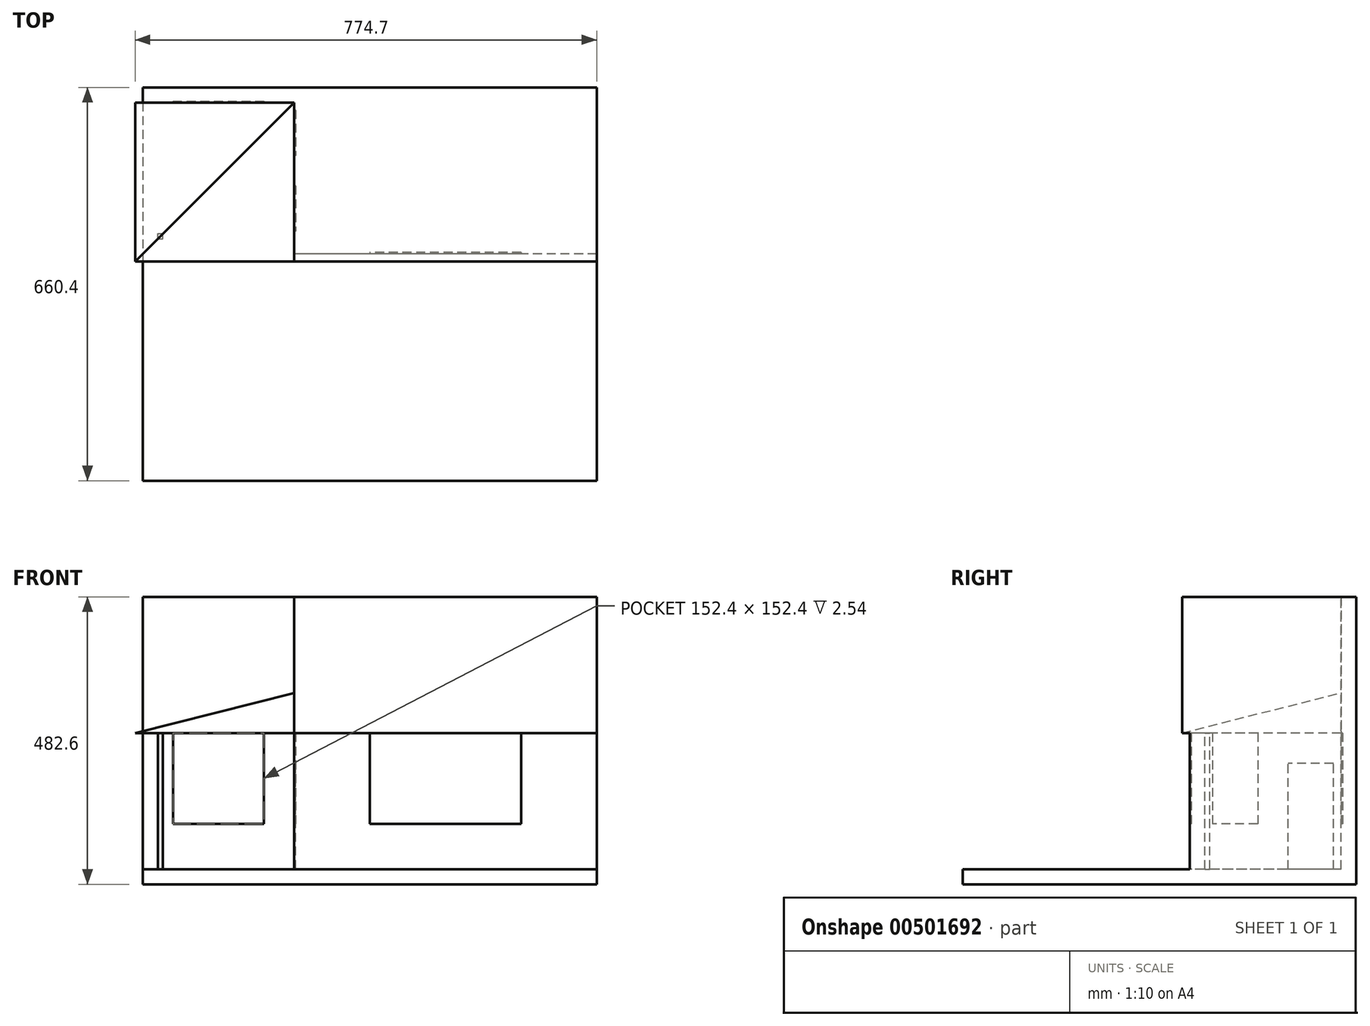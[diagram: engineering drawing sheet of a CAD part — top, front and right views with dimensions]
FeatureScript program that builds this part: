
annotation { "Feature Type Name" : "Feature", "Feature Type Description" : "" }
export const myFeature = defineFeature(function(context is Context, id is Id, definition is map)
    precondition{}
    {
        {
            var Q0;
            Q0=qCreatedBy(makeId("Top.planeOp"),FACE);
            var sketch = newSketch(context, id + "F0", { "sketchPlane" : qUnion([Q0])});
            skLineSegment(sketch, "E0.bottom", {"start": v(381, 330.2) * mm, "end": v(-381, 330.2) * mm});
            skLineSegment(sketch, "E0.top", {"start": v(381, -330.2) * mm, "end": v(-381, -330.2) * mm});
            skLineSegment(sketch, "E0.left", {"start": v(381, 330.2) * mm, "end": v(381, -330.2) * mm});
            skLineSegment(sketch, "E0.right", {"start": v(-381, 330.2) * mm, "end": v(-381, -330.2) * mm});
            skPoint(sketch, "E0.middle", {"position": v(0, 0) * mm});
            skSolve(sketch);
        }
        {
            var Q0;
            Q0 = qSketchRegion(id + "F0", true);
            extrude(context, id + "F1", {"entities" : qUnion([Q0]), "oppositeDirection" : true, "depth" : 25.4 * mm});
        }
        {
            var Q0;
            Q0=makeQuery(id+"F0.imprint","IMPRINT",FACE,{"disambiguationData":[TD([[makeQuery(id+"F0.imprint","IMPRINT",EDGE,{"derivedFrom":sQuery(id+"F0.wireOp",EDGE,"E0.bottom")}),1.0]])]});
            var sketch = newSketch(context, id + "F2", { "sketchPlane" : qUnion([Q0])});
            skLineSegment(sketch, "E1.bottom", {"start": v(381, 330.2) * mm, "end": v(-127, 330.2) * mm});
            skLineSegment(sketch, "E1.top", {"start": v(381, 50.8) * mm, "end": v(-127, 50.8) * mm});
            skLineSegment(sketch, "E1.left", {"start": v(381, 330.2) * mm, "end": v(381, 50.8) * mm});
            skLineSegment(sketch, "E1.right", {"start": v(-127, 330.2) * mm, "end": v(-127, 50.8) * mm});
            skSolve(sketch);
        }
        {
            var Q0;
            Q0 = qSketchRegion(id + "F2", true);
            extrude(context, id + "F3", {"entities" : qUnion([Q0]), "operationType" : NewBodyOperationType.ADD, "depth" : 228.6 * mm});
        }
        {
            var Q0;
            Q0=makeQuery(id+"F3.opExtrude","SWEPT_FACE",FACE,{"disambiguationData":[OSD([sQuery(id+"F2.wireOp",EDGE,"E1.top")])]});
            var sketch = newSketch(context, id + "F4", { "sketchPlane" : qUnion([Q0])});
            skLineSegment(sketch, "E2.bottom", {"start": v(254, 228.6) * mm, "end": v(0, 228.6) * mm});
            skLineSegment(sketch, "E2.top", {"start": v(254, 76.2) * mm, "end": v(0, 76.2) * mm});
            skLineSegment(sketch, "E2.left", {"start": v(254, 228.6) * mm, "end": v(254, 76.2) * mm});
            skLineSegment(sketch, "E2.right", {"start": v(0, 228.6) * mm, "end": v(0, 76.2) * mm});
            skSolve(sketch);
        }
        {
            var Q0;
            Q0 = qSketchRegion(id + "F4", true);
            extrude(context, id + "F5", {"entities" : qUnion([Q0]), "operationType" : NewBodyOperationType.REMOVE, "oppositeDirection" : true, "depth" : 2.54 * mm});
        }
        {
            var Q0;
            Q0=makeQuery(id+"F3.boolean.opBoolean","MERGE",FACE,{"derivedFrom":[makeQuery(id+"F1.opExtrude","SWEPT_FACE",FACE,{"disambiguationData":[OSD([sQuery(id+"F0.wireOp",EDGE,"E0.bottom")])]}),makeQuery(id+"F3.opExtrude","SWEPT_FACE",FACE,{"disambiguationData":[OSD([sQuery(id+"F2.wireOp",EDGE,"E1.bottom")])]})]});
            var sketch = newSketch(context, id + "F6", { "sketchPlane" : qUnion([Q0])});
            skLineSegment(sketch, "E3.bottom", {"start": v(127, 0) * mm, "end": v(381, 0) * mm});
            skLineSegment(sketch, "E3.top", {"start": v(127, 228.6) * mm, "end": v(381, 228.6) * mm});
            skLineSegment(sketch, "E3.left", {"start": v(127, 0) * mm, "end": v(127, 228.6) * mm});
            skLineSegment(sketch, "E3.right", {"start": v(381, 0) * mm, "end": v(381, 228.6) * mm});
            skSolve(sketch);
        }
        {
            var Q0;
            Q0 = qSketchRegion(id + "F6", true);
            extrude(context, id + "F7", {"entities" : qUnion([Q0]), "oppositeDirection" : true, "depth" : 25.4 * mm});
        }
        {
            var Q0;
            Q0=makeQuery(id+"F3.opExtrude","SWEPT_FACE",FACE,{"disambiguationData":[OSD([sQuery(id+"F2.wireOp",EDGE,"E1.right")])]});
            var sketch = newSketch(context, id + "F8", { "sketchPlane" : qUnion([Q0])});
            skLineSegment(sketch, "E4.bottom", {"start": v(-165.1, 228.6) * mm, "end": v(-88.9, 228.6) * mm});
            skLineSegment(sketch, "E4.top", {"start": v(-165.1, 76.2) * mm, "end": v(-88.9, 76.2) * mm});
            skLineSegment(sketch, "E4.left", {"start": v(-165.1, 228.6) * mm, "end": v(-165.1, 76.2) * mm});
            skLineSegment(sketch, "E4.right", {"start": v(-88.9, 228.6) * mm, "end": v(-88.9, 76.2) * mm});
            skLineSegment(sketch, "E5.bottom", {"start": v(-292.1, 0) * mm, "end": v(-215.9, 0) * mm});
            skLineSegment(sketch, "E5.top", {"start": v(-292.1, 177.8) * mm, "end": v(-215.9, 177.8) * mm});
            skLineSegment(sketch, "E5.left", {"start": v(-292.1, 0) * mm, "end": v(-292.1, 177.8) * mm});
            skLineSegment(sketch, "E5.right", {"start": v(-215.9, 0) * mm, "end": v(-215.9, 177.8) * mm});
            skSolve(sketch);
        }
        {
            var Q0;
            Q0 = qSketchRegion(id + "F8", true);
            extrude(context, id + "F9", {"entities" : qUnion([Q0]), "operationType" : NewBodyOperationType.REMOVE, "oppositeDirection" : true, "depth" : 2.54 * mm});
        }
        {
            var Q0;
            Q0=makeQuery(id+"F7.opExtrude","SWEPT_BODY",BODY,{"disambiguationData":[OSD([sQuery(id+"F6.wireOp",EDGE,"E3.bottom"),sQuery(id+"F6.wireOp",EDGE,"E3.top"),sQuery(id+"F6.wireOp",EDGE,"E3.left"),sQuery(id+"F6.wireOp",EDGE,"E3.right")])]});
            var Q1;
            Q1=makeQuery(id+"F1.opExtrude","SWEPT_BODY",BODY,{"disambiguationData":[OSD([sQuery(id+"F0.wireOp",EDGE,"E0.bottom"),sQuery(id+"F0.wireOp",EDGE,"E0.top"),sQuery(id+"F0.wireOp",EDGE,"E0.left"),sQuery(id+"F0.wireOp",EDGE,"E0.right")])]});
            booleanBodies(context, id + "F10", {"operationType" : BooleanOperationType.UNION, "tools" : qUnion([Q0, Q1])});
        }
        {
            var Q0;
            Q0=makeQuery(id+"F7.opExtrude","CAP_FACE",FACE,{"disambiguationData":[OSD([sQuery(id+"F6.wireOp",EDGE,"E3.bottom"),sQuery(id+"F6.wireOp",EDGE,"E3.top"),sQuery(id+"F6.wireOp",EDGE,"E3.left"),sQuery(id+"F6.wireOp",EDGE,"E3.right")])],"isStart":false});
            var sketch = newSketch(context, id + "F11", { "sketchPlane" : qUnion([Q0])});
            skLineSegment(sketch, "E6.bottom", {"start": v(-330.2, 228.6) * mm, "end": v(-177.8, 228.6) * mm});
            skLineSegment(sketch, "E6.top", {"start": v(-330.2, 76.2) * mm, "end": v(-177.8, 76.2) * mm});
            skLineSegment(sketch, "E6.left", {"start": v(-330.2, 228.6) * mm, "end": v(-330.2, 76.2) * mm});
            skLineSegment(sketch, "E6.right", {"start": v(-177.8, 228.6) * mm, "end": v(-177.8, 76.2) * mm});
            skSolve(sketch);
        }
        {
            var Q0;
            Q0 = qSketchRegion(id + "F11", true);
            extrude(context, id + "F12", {"entities" : qUnion([Q0]), "operationType" : NewBodyOperationType.REMOVE, "oppositeDirection" : true, "depth" : 2.54 * mm});
        }
        {
            var Q0;
            Q0=makeQuery(id+"F10.opBoolean","MERGE",FACE,{"derivedFrom":[makeQuery(id+"F7.opExtrude","SWEPT_FACE",FACE,{"disambiguationData":[OSD([sQuery(id+"F6.wireOp",EDGE,"E3.top")])]}),makeQuery(id+"F3.opExtrude","CAP_FACE",FACE,{"disambiguationData":[OSD([sQuery(id+"F2.wireOp",EDGE,"E1.bottom"),sQuery(id+"F2.wireOp",EDGE,"E1.top"),sQuery(id+"F2.wireOp",EDGE,"E1.left"),sQuery(id+"F2.wireOp",EDGE,"E1.right")])],"isStart":false})]});
            var sketch = newSketch(context, id + "F13", { "sketchPlane" : qUnion([Q0])});
            skLineSegment(sketch, "E7.bottom", {"start": v(381, 330.2) * mm, "end": v(-127, 330.2) * mm});
            skLineSegment(sketch, "E7.top", {"start": v(381, 38.1) * mm, "end": v(-127, 38.1) * mm});
            skLineSegment(sketch, "E7.left", {"start": v(381, 330.2) * mm, "end": v(381, 38.1) * mm});
            skLineSegment(sketch, "E7.right", {"start": v(-127, 330.2) * mm, "end": v(-127, 38.1) * mm});
            skSolve(sketch);
        }
        {
            var Q0;
            Q0 = qSketchRegion(id + "F13", true);
            extrude(context, id + "F14", {"entities" : qUnion([Q0]), "operationType" : NewBodyOperationType.ADD, "depth" : 228.6 * mm});
        }
        {
            var Q0;
            Q0=makeQuery(id+"F14.boolean.opBoolean","MERGE",FACE,{"derivedFrom":[makeQuery(id+"F3.opExtrude","SWEPT_FACE",FACE,{"disambiguationData":[OSD([sQuery(id+"F2.wireOp",EDGE,"E1.right")])]}),makeQuery(id+"F14.opExtrude","SWEPT_FACE",FACE,{"disambiguationData":[OSD([sQuery(id+"F13.wireOp",EDGE,"E7.right")])]})]});
            var sketch = newSketch(context, id + "F15", { "sketchPlane" : qUnion([Q0])});
            skLineSegment(sketch, "E8", {"start": v(-304.8, 228.6) * mm, "end": v(-38.1, 228.6) * mm});
            skLineSegment(sketch, "E9", {"start": v(-38.1, 228.6) * mm, "end": v(-304.8, 295.97) * mm});
            skLineSegment(sketch, "E10", {"start": v(-304.8, 295.97) * mm, "end": v(-304.8, 228.6) * mm});
            skSolve(sketch);
        }
        {
            var Q0;
            Q0=makeQuery(id+"F10.opBoolean","MERGE",FACE,{"derivedFrom":[makeQuery(id+"F7.opExtrude","SWEPT_FACE",FACE,{"disambiguationData":[OSD([sQuery(id+"F6.wireOp",EDGE,"E3.top")])]}),makeQuery(id+"F3.opExtrude","CAP_FACE",FACE,{"disambiguationData":[OSD([sQuery(id+"F2.wireOp",EDGE,"E1.bottom"),sQuery(id+"F2.wireOp",EDGE,"E1.top"),sQuery(id+"F2.wireOp",EDGE,"E1.left"),sQuery(id+"F2.wireOp",EDGE,"E1.right")])],"isStart":false})]});
            var sketch = newSketch(context, id + "F16", { "sketchPlane" : qUnion([Q0])});
            skLineSegment(sketch, "E11.bottom", {"start": v(-127, 330.2) * mm, "end": v(-381, 330.2) * mm});
            skLineSegment(sketch, "E11.top", {"start": v(-127, 304.8) * mm, "end": v(-381, 304.8) * mm});
            skLineSegment(sketch, "E11.left", {"start": v(-127, 330.2) * mm, "end": v(-127, 304.8) * mm});
            skLineSegment(sketch, "E11.right", {"start": v(-381, 330.2) * mm, "end": v(-381, 304.8) * mm});
            skSolve(sketch);
        }
        {
            var Q0;
            Q0 = qSketchRegion(id + "F16", true);
            extrude(context, id + "F17", {"entities" : qUnion([Q0]), "operationType" : NewBodyOperationType.ADD, "depth" : 228.6 * mm});
        }
        {
            var Q0;
            Q0 = qSketchRegion(id + "F15", true);
            extrude(context, id + "F18", {"entities" : qUnion([Q0]), "operationType" : NewBodyOperationType.ADD, "depth" : 266.7 * mm});
        }
        {
            var Q0;
            Q0=makeQuery(id+"F18.opExtrude","SWEPT_FACE",FACE,{"disambiguationData":[OSD([sQuery(id+"F15.wireOp",EDGE,"E10")])]});
            var sketch = newSketch(context, id + "F19", { "sketchPlane" : qUnion([Q0])});
            skLineSegment(sketch, "E12", {"start": v(393.7, 228.6) * mm, "end": v(393.7, 295.97) * mm});
            skLineSegment(sketch, "E13", {"start": v(393.7, 295.97) * mm, "end": v(127, 295.97) * mm});
            skLineSegment(sketch, "E14", {"start": v(127, 295.97) * mm, "end": v(393.7, 228.6) * mm});
            skSolve(sketch);
        }
        {
            var Q0;
            Q0 = qSketchRegion(id + "F19", true);
            extrude(context, id + "F20", {"entities" : qUnion([Q0]), "operationType" : NewBodyOperationType.REMOVE, "endBound" : BoundingType.UP_TO_NEXT, "oppositeDirection" : true, "depth" : 25.4 * mm});
        }
        {
            var Q0;
            {var subQ1=sQuery(id+"F13.wireOp",EDGE,"E7.right");var subQ3=sQuery(id+"F8.wireOp",EDGE,"E4.left");var subQ5=sQuery(id+"F13.wireOp",EDGE,"E7.left");var subQ6=sQuery(id+"F13.wireOp",EDGE,"E7.top");var subQ7=makeQuery(id+"F14.opExtrude","CAP_FACE",FACE,{"disambiguationData":[OSD([sQuery(id+"F13.wireOp",EDGE,"E7.bottom"),subQ6,subQ5,subQ1])],"isStart":true});Q0=makeQuery(id+"F18.boolean.opBoolean","MERGE",FACE,{"derivedFrom":[makeQuery(id+"F14.boolean.opBoolean","SPLIT",FACE,{"disambiguationData":[TD([makeQuery(id+"F1.opExtrude","SWEPT_FACE",FACE,{"disambiguationData":[OSD([sQuery(id+"F0.wireOp",EDGE,"E0.left")])]})])],"derivedFrom":subQ7}),makeQuery(id+"F14.boolean.opBoolean","SPLIT",FACE,{"disambiguationData":[TD([makeQuery(id+"F9.boolean.opBoolean","COPY",FACE,{"derivedFrom":makeQuery(id+"F9.opExtrude","SWEPT_FACE",FACE,{"disambiguationData":[OSD([subQ3])]})})])],"derivedFrom":subQ7}),makeQuery(id+"F17.opExtrude","CAP_FACE",FACE,{"disambiguationData":[OSD([sQuery(id+"F16.wireOp",EDGE,"E11.bottom"),sQuery(id+"F16.wireOp",EDGE,"E11.top"),sQuery(id+"F16.wireOp",EDGE,"E11.left"),sQuery(id+"F16.wireOp",EDGE,"E11.right")])],"isStart":true}),makeQuery(id+"F18.opExtrude","SWEPT_FACE",FACE,{"disambiguationData":[OSD([sQuery(id+"F15.wireOp",EDGE,"E8")])]})]});}
            var sketch = newSketch(context, id + "F21", { "sketchPlane" : qUnion([Q0])});
            skLineSegment(sketch, "E15.bottom", {"start": v(-355.6, -76.2) * mm, "end": v(-347.22, -76.2) * mm});
            skLineSegment(sketch, "E15.top", {"start": v(-355.6, -84.58) * mm, "end": v(-347.22, -84.58) * mm});
            skLineSegment(sketch, "E15.left", {"start": v(-355.6, -76.2) * mm, "end": v(-355.6, -84.58) * mm});
            skLineSegment(sketch, "E15.right", {"start": v(-347.22, -76.2) * mm, "end": v(-347.22, -84.58) * mm});
            skSolve(sketch);
        }
        {
            var Q0;
            Q0 = qSketchRegion(id + "F21", true);
            extrude(context, id + "F22", {"entities" : qUnion([Q0]), "operationType" : NewBodyOperationType.ADD, "depth" : 228.6 * mm});
        }
    });
